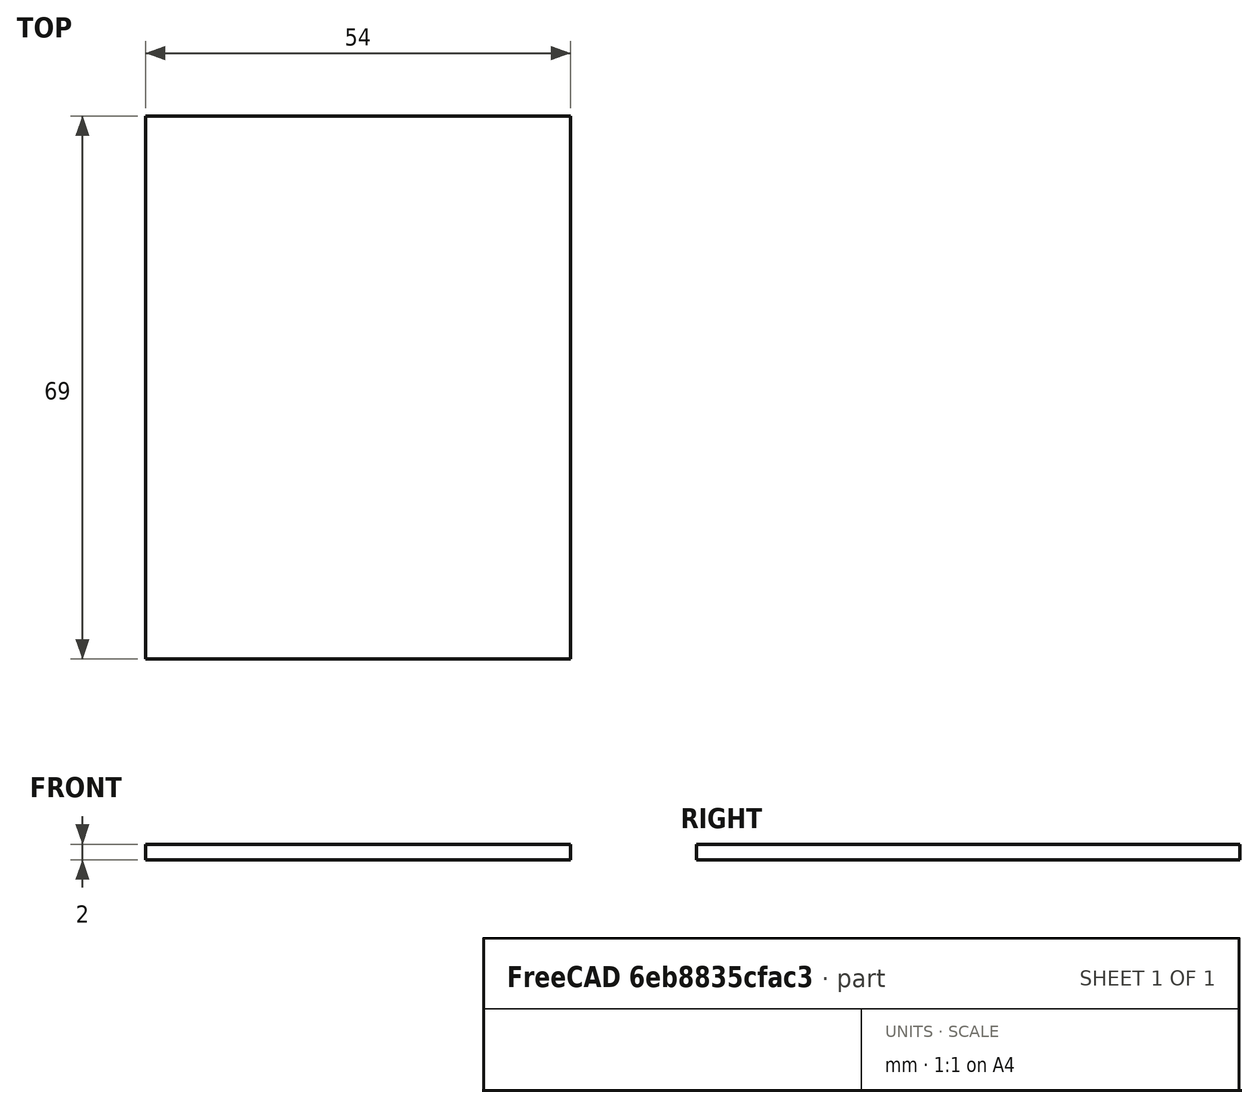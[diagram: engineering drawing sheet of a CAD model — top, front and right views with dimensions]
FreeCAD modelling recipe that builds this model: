
FCSTD DOCUMENT  (FreeCAD 1.0R39319 (Git))
Label: nano-breakout
License: All rights reserved
LicenseURL: http://en.wikipedia.org/wiki/All_rights_reserved
objects: Sketcher::SketchObject×1, Spreadsheet::Sheet×1, PartDesign::Pad×1, PartDesign::Body×1
note: 6 computed .brp shape members not serialized (recipe doc carries the construction recipe); baked Part::Feature solids carry a one-line shape summary decoded from their .brp

FEATURE [Sketcher::SketchObject] Sketch
  ArcFitTolerance = 1e-06
  AttachmentSupport = -> [XY_Plane]
  FullyConstrained = true
  MakeInternals = false
  MapMode = 5
  expr: Constraints[8] = Spreadsheet.width
  expr: Constraints[9] = Spreadsheet.length
  sketch-geometry (4):
    g0: LineSegment StartX=30 StartY=66 StartZ=0 EndX=30 EndY=-3 EndZ=0
    g1: LineSegment StartX=30 StartY=-3 StartZ=0 EndX=84 EndY=-3 EndZ=0
    g2: LineSegment StartX=84 StartY=-3 StartZ=0 EndX=84 EndY=66 EndZ=0
    g3: LineSegment StartX=84 StartY=66 StartZ=0 EndX=30 EndY=66 EndZ=0
  constraints (12):
    c: Coincident(g0,g1)
    c: Coincident(g1,g2)
    c: Coincident(g2,g3)
    c: Coincident(g3,g0)
    c: Vertical(g0)
    c: Vertical(g2)
    c: Horizontal(g1)
    c: Horizontal(g3)
    c: DistanceX(g0,g1) = 54
    c: DistanceY(g0,g0) = 69
    c: DistanceX(g-1,g0) = 30
    c: DistanceY(g0,g-1) = 3
FEATURE [Spreadsheet::Sheet] Spreadsheet
  cells = A2='width; B2(width)=54; A3='length; B3(length)=69; A4='height; B4(height)=2
FEATURE [PartDesign::Pad] Pad
  Direction = (0,0,1)
  Length = 2
  Length2 = 10
  Profile = -> Sketch
  ReferenceAxis = -> Sketch [N_Axis]
  Suppressed = false
  Type = 0
  expr: Length = Spreadsheet.height
FEATURE [PartDesign::Body] Body
  AllowCompound = false
  Group = -> [Sketch,Pad]
  Origin = -> Origin
  Tip = -> Pad
